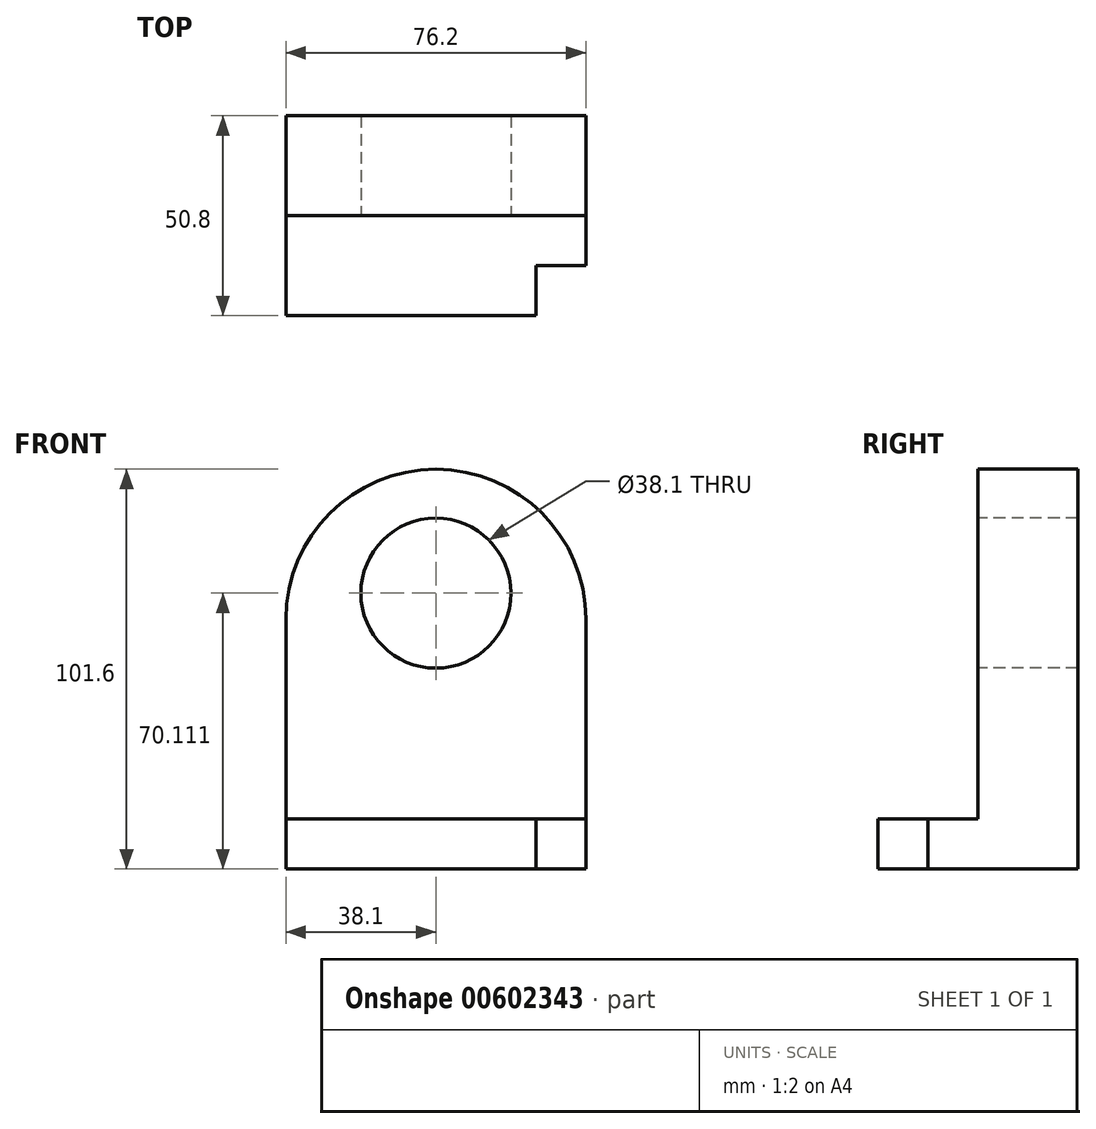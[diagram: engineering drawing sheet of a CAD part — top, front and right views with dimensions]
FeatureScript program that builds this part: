
annotation { "Feature Type Name" : "Feature", "Feature Type Description" : "" }
export const myFeature = defineFeature(function(context is Context, id is Id, definition is map)
    precondition{}
    {
        {
            var Q0;
            Q0=qCreatedBy(makeId("Top.planeOp"),FACE);
            var sketch = newSketch(context, id + "F0", { "sketchPlane" : qUnion([Q0])});
            skLineSegment(sketch, "E0.bottom", {"start": v(-38.1, 25.4) * mm, "end": v(38.1, 25.4) * mm});
            skLineSegment(sketch, "E0.top", {"start": v(-38.1, -25.4) * mm, "end": v(38.1, -25.4) * mm});
            skLineSegment(sketch, "E0.left", {"start": v(-38.1, 25.4) * mm, "end": v(-38.1, -25.4) * mm});
            skLineSegment(sketch, "E0.right", {"start": v(38.1, 25.4) * mm, "end": v(38.1, -25.4) * mm});
            skPoint(sketch, "E0.middle", {"position": v(0, 0) * mm});
            skSolve(sketch);
        }
        {
            var Q0;
            Q0=makeQuery(id+"F0.imprint","IMPRINT",FACE,{"disambiguationData":[TD([[makeQuery(id+"F0.imprint","IMPRINT",EDGE,{"derivedFrom":sQuery(id+"F0.wireOp",EDGE,"E0.bottom")}),-1.0]])]});
            extrude(context, id + "F1", {"entities" : qUnion([Q0]), "depth" : 12.7 * mm, "offsetDistance" : 25.4 * mm});
        }
        {
            var Q0;
            Q0=makeQuery(id+"F1.opExtrude","CAP_FACE",FACE,{"disambiguationData":[OSD([sQuery(id+"F0.wireOp",EDGE,"E0.bottom"),sQuery(id+"F0.wireOp",EDGE,"E0.top"),sQuery(id+"F0.wireOp",EDGE,"E0.left"),sQuery(id+"F0.wireOp",EDGE,"E0.right")])],"isStart":false});
            var sketch = newSketch(context, id + "F2", { "sketchPlane" : qUnion([Q0])});
            skLineSegment(sketch, "E1.bottom", {"start": v(38.1, -25.4) * mm, "end": v(25.4, -25.4) * mm});
            skLineSegment(sketch, "E1.top", {"start": v(38.1, -12.7) * mm, "end": v(25.4, -12.7) * mm});
            skLineSegment(sketch, "E1.left", {"start": v(38.1, -25.4) * mm, "end": v(38.1, -12.7) * mm});
            skLineSegment(sketch, "E1.right", {"start": v(25.4, -25.4) * mm, "end": v(25.4, -12.7) * mm});
            skSolve(sketch);
        }
        {
            var Q0;
            Q0 = qSketchRegion(id + "F2", true);
            extrude(context, id + "F3", {"entities" : qUnion([Q0]), "operationType" : NewBodyOperationType.REMOVE, "oppositeDirection" : true, "depth" : 12.7 * mm, "offsetDistance" : 25.4 * mm});
        }
        {
            var Q0;
            Q0=qCreatedBy(makeId("Front.planeOp"),FACE);
            var sketch = newSketch(context, id + "F4", { "sketchPlane" : qUnion([Q0])});
            skLineSegment(sketch, "E2.bottom", {"start": v(38.1, 12.7) * mm, "end": v(-38.1, 12.7) * mm});
            skLineSegment(sketch, "E2.top", {"start": v(38.1, 63.5) * mm, "end": v(-38.1, 63.5) * mm});
            skLineSegment(sketch, "E2.left", {"start": v(38.1, 12.7) * mm, "end": v(38.1, 63.5) * mm});
            skLineSegment(sketch, "E2.right", {"start": v(-38.1, 12.7) * mm, "end": v(-38.1, 63.5) * mm});
            skCircle(sketch, "E3", {"center": v(0, 63.5) * mm, "radius": 38.1 * mm});
            skSolve(sketch);
        }
        {
            var Q0;
            Q0=makeQuery(id+"F4.imprint","IMPRINT",FACE,{"disambiguationData":[TD([[makeQuery(id+"F4.imprint","IMPRINT",EDGE,{"derivedFrom":sQuery(id+"F4.wireOp",EDGE,"E2.bottom")}),-1.0]])]});
            var Q1;
            {var subQ0=sQuery(id+"F4.wireOp",EDGE,"E2.top");Q1=makeQuery(id+"F4.imprint","IMPRINT",FACE,{"disambiguationData":[TD([[makeQuery(id+"F4.imprint","IMPRINT",EDGE,{"derivedFrom":subQ0}),1.0]])]});}
            var Q2;
            {var subQ0=sQuery(id+"F4.wireOp",EDGE,"E2.top");Q2=makeQuery(id+"F4.imprint","IMPRINT",FACE,{"disambiguationData":[TD([[makeQuery(id+"F4.imprint","IMPRINT",EDGE,{"derivedFrom":subQ0}),-1.0]])]});}
            extrude(context, id + "F5", {"entities" : qUnion([Q0, Q1, Q2]), "operationType" : NewBodyOperationType.ADD, "oppositeDirection" : true, "depth" : 25.4 * mm, "offsetDistance" : 25.4 * mm});
        }
        {
            var Q0;
            Q0=makeQuery(id+"F5.opExtrude","CAP_FACE",FACE,{"disambiguationData":[OSD([sQuery(id+"F4.wireOp",EDGE,"E2.bottom"),sQuery(id+"F4.wireOp",EDGE,"E2.left"),sQuery(id+"F4.wireOp",EDGE,"E2.right"),sQuery(id+"F4.wireOp",EDGE,"E3")])],"isStart":true});
            var sketch = newSketch(context, id + "F6", { "sketchPlane" : qUnion([Q0])});
            skCircle(sketch, "E4", {"center": v(0, 70.11) * mm, "radius": 19.05 * mm});
            skSolve(sketch);
        }
        {
            var Q0;
            Q0 = qSketchRegion(id + "F6", true);
            extrude(context, id + "F7", {"entities" : qUnion([Q0]), "operationType" : NewBodyOperationType.REMOVE, "oppositeDirection" : true, "depth" : 25.4 * mm, "offsetDistance" : 25.4 * mm});
        }
    });
